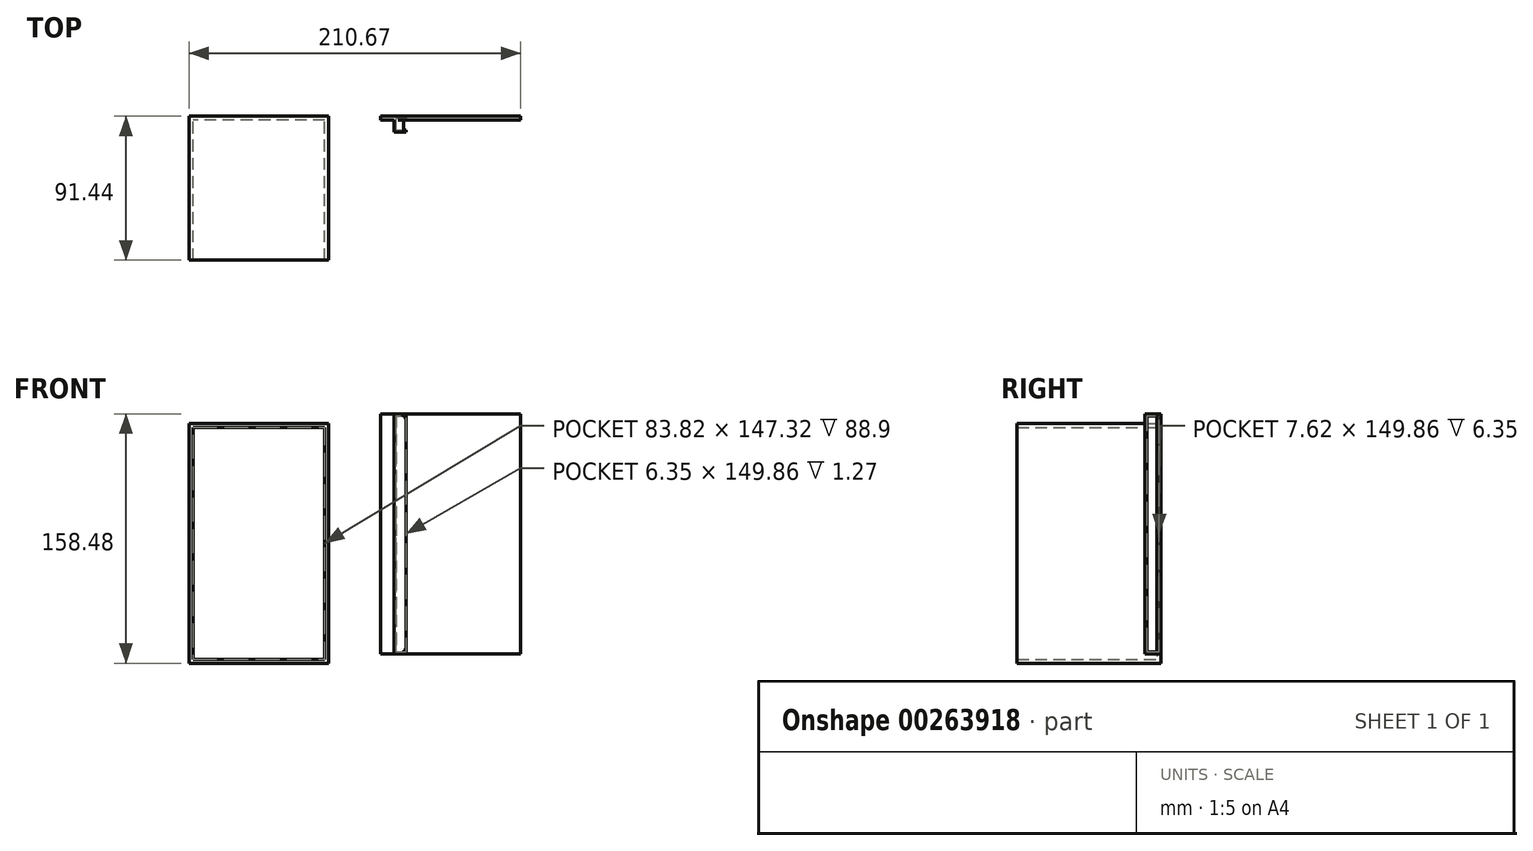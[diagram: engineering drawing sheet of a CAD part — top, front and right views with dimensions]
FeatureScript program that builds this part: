
annotation { "Feature Type Name" : "Feature", "Feature Type Description" : "" }
export const myFeature = defineFeature(function(context is Context, id is Id, definition is map)
    precondition{}
    {
        {
            var Q0;
            Q0=qCreatedBy(makeId("Front.planeOp"),FACE);
            var sketch = newSketch(context, id + "F0", { "sketchPlane" : qUnion([Q0])});
            skLineSegment(sketch, "E0.bottom", {"start": v(44.45, 76.2) * mm, "end": v(-44.45, 76.2) * mm});
            skLineSegment(sketch, "E0.top", {"start": v(44.45, -76.2) * mm, "end": v(-44.45, -76.2) * mm});
            skLineSegment(sketch, "E0.left", {"start": v(44.45, 76.2) * mm, "end": v(44.45, -76.2) * mm});
            skLineSegment(sketch, "E0.right", {"start": v(-44.45, 76.2) * mm, "end": v(-44.45, -76.2) * mm});
            skPoint(sketch, "E0.middle", {"position": v(0, 0) * mm});
            skSolve(sketch);
        }
        {
            var Q0;
            Q0=qCreatedBy(makeId("Front.planeOp"),FACE);
            var sketch = newSketch(context, id + "F1", { "sketchPlane" : qUnion([Q0])});
            skLineSegment(sketch, "E1.bottom", {"start": v(77.32, -70.12) * mm, "end": v(166.22, -70.12) * mm});
            skLineSegment(sketch, "E1.top", {"start": v(77.32, 82.28) * mm, "end": v(166.22, 82.28) * mm});
            skLineSegment(sketch, "E1.left", {"start": v(77.32, -70.12) * mm, "end": v(77.32, 82.28) * mm});
            skLineSegment(sketch, "E1.right", {"start": v(166.22, -70.12) * mm, "end": v(166.22, 82.28) * mm});
            skSolve(sketch);
        }
        {
            var Q0;
            Q0=makeQuery(id+"F0.imprint","IMPRINT",FACE,{"disambiguationData":[TD([[makeQuery(id+"F0.imprint","IMPRINT",EDGE,{"derivedFrom":sQuery(id+"F0.wireOp",EDGE,"E0.bottom")}),1.0]])]});
            extrude(context, id + "F2", {"entities" : qUnion([Q0]), "depth" : 88.9 * mm});
        }
        {
            var Q0;
            Q0=makeQuery(id+"F1.imprint","IMPRINT",FACE,{"disambiguationData":[TD([[makeQuery(id+"F1.imprint","IMPRINT",EDGE,{"derivedFrom":sQuery(id+"F1.wireOp",EDGE,"E1.bottom")}),1.0]])]});
            var Q1;
            Q1=makeQuery(id+"F2.opExtrude","CAP_FACE",FACE,{"disambiguationData":[OSD([sQuery(id+"F0.wireOp",EDGE,"E0.bottom"),sQuery(id+"F0.wireOp",EDGE,"E0.top"),sQuery(id+"F0.wireOp",EDGE,"E0.left"),sQuery(id+"F0.wireOp",EDGE,"E0.right")])],"isStart":false});
            extrude(context, id + "F3", {"entities" : qUnion([Q0, Q1]), "operationType" : NewBodyOperationType.ADD, "depth" : 2.54 * mm});
        }
        {
            var Q0;
            Q0=makeQuery(id+"F3.opExtrude","CAP_FACE",FACE,{"disambiguationData":[OSD([sQuery(id+"F1.wireOp",EDGE,"E1.bottom"),sQuery(id+"F1.wireOp",EDGE,"E1.top"),sQuery(id+"F1.wireOp",EDGE,"E1.left"),sQuery(id+"F1.wireOp",EDGE,"E1.right")])],"isStart":false});
            var sketch = newSketch(context, id + "F4", { "sketchPlane" : qUnion([Q0])});
            skLineSegment(sketch, "E2.bottom", {"start": v(85.95, 82.28) * mm, "end": v(93.57, 82.28) * mm});
            skLineSegment(sketch, "E2.top", {"start": v(85.95, -70.12) * mm, "end": v(93.57, -70.12) * mm});
            skLineSegment(sketch, "E2.left", {"start": v(85.95, 82.28) * mm, "end": v(85.95, -70.12) * mm});
            skLineSegment(sketch, "E2.right", {"start": v(93.57, 82.28) * mm, "end": v(93.57, -70.12) * mm});
            skSolve(sketch);
        }
        {
            var Q0;
            Q0 = qSketchRegion(id + "F4", true);
            extrude(context, id + "F5", {"entities" : qUnion([Q0]), "operationType" : NewBodyOperationType.ADD, "depth" : 7.62 * mm});
        }
        {
            var Q0;
            Q0=makeQuery(id+"F3.opExtrude","CAP_FACE",FACE,{"disambiguationData":[OSD([sQuery(id+"F0.wireOp",EDGE,"E0.bottom"),sQuery(id+"F0.wireOp",EDGE,"E0.top"),sQuery(id+"F0.wireOp",EDGE,"E0.left"),sQuery(id+"F0.wireOp",EDGE,"E0.right")])],"isStart":false});
            shell(context, id + "F6", {"entities" : qUnion([Q0]), "thickness" : 2.54 * mm});
        }
        {
            var Q0;
            Q0=makeQuery(id+"F5.opExtrude","SWEPT_FACE",FACE,{"disambiguationData":[OSD([sQuery(id+"F4.wireOp",EDGE,"E2.right")])]});
            shell(context, id + "F7", {"entities" : qUnion([Q0]), "thickness" : 1.27 * mm});
        }
        {
            var Q0;
            Q0=makeQuery(id+"F5.opExtrude","SWEPT_EDGE",EDGE,{"disambiguationData":[OSD([sQuery(id+"F1.wireOp",EDGE,"E1.top"),sQuery(id+"F4.wireOp",EDGE,"E2.bottom"),sQuery(id+"F4.wireOp",EDGE,"E2.right")])]});
            var Q1;
            Q1=makeQuery(id+"F5.opExtrude","SWEPT_EDGE",EDGE,{"disambiguationData":[OSD([sQuery(id+"F1.wireOp",EDGE,"E1.bottom"),sQuery(id+"F4.wireOp",EDGE,"E2.top"),sQuery(id+"F4.wireOp",EDGE,"E2.right")])]});
            fillet(context, id + "F8", {"entities" : qUnion([Q0, Q1]), "radius" : 5.08 * mm, "tangentPropagation" : true, "allowEdgeOverflow" : false});
        }
    });
